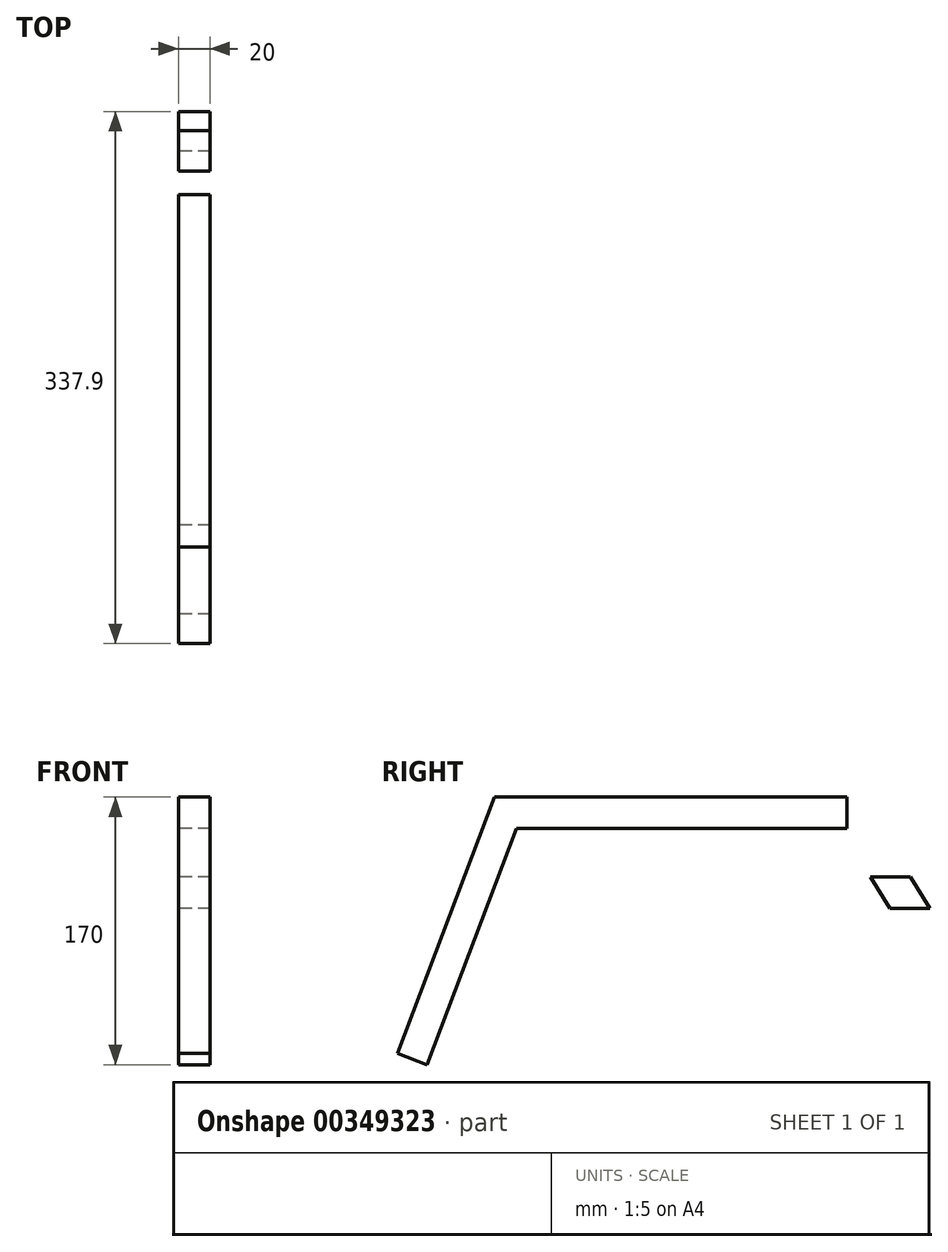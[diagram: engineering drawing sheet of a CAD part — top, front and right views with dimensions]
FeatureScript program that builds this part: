
annotation { "Feature Type Name" : "Feature", "Feature Type Description" : "" }
export const myFeature = defineFeature(function(context is Context, id is Id, definition is map)
    precondition{}
    {
        {
            var Q0;
            Q0=qCreatedBy(makeId("Right.planeOp"),FACE);
            var sketch = newSketch(context, id + "F0", { "sketchPlane" : qUnion([Q0])});
            skLineSegment(sketch, "E0", {"start": v(241, -95.83) * mm, "end": v(224.34, -106.9) * mm});
            skLineSegment(sketch, "E1", {"start": v(241, -95.83) * mm, "end": v(217.72, -95.83) * mm});
            skLineSegment(sketch, "E2", {"start": v(241, -95.83) * mm, "end": v(-76.2, -95.83) * mm});
            skLineSegment(sketch, "E3", {"start": v(-76.2, -95.83) * mm, "end": v(-76.2, 44.17) * mm});
            skLineSegment(sketch, "E4", {"start": v(-76.2, 44.17) * mm, "end": v(-76.2, 24.17) * mm});
            skLineSegment(sketch, "E5", {"start": v(-76.2, 24.17) * mm, "end": v(328.64, 24.17) * mm});
            skLineSegment(sketch, "E6", {"start": v(-76.2, 44.17) * mm, "end": v(348.84, 44.17) * mm});
            skLineSegment(sketch, "E7", {"start": v(241, -95.83) * mm, "end": v(139.09, 70.9) * mm});
            skLineSegment(sketch, "E8", {"start": v(224.34, -106.9) * mm, "end": v(129.89, 44.17) * mm});
            skLineSegment(sketch, "E9", {"start": v(129.89, 44.17) * mm, "end": v(148.48, 55.53) * mm});
            skSolve(sketch);
        }
        {
            var Q0;
            Q0=qCreatedBy(makeId("Right.planeOp"),FACE);
            var sketch = newSketch(context, id + "F1", { "sketchPlane" : qUnion([Q0])});
            skLineSegment(sketch, "E10.bottom", {"start": v(-95, 75) * mm, "end": v(95, 75) * mm});
            skLineSegment(sketch, "E10.top", {"start": v(-95, -75) * mm, "end": v(95, -75) * mm});
            skLineSegment(sketch, "E10.left", {"start": v(-95, 75) * mm, "end": v(-95, -75) * mm});
            skLineSegment(sketch, "E10.right", {"start": v(95, 75) * mm, "end": v(95, -75) * mm});
            skPoint(sketch, "E10.middle", {"position": v(0, 0) * mm});
            skLineSegment(sketch, "E11", {"start": v(-95, 75) * mm, "end": v(-151.54, -75) * mm});
            skLineSegment(sketch, "E12", {"start": v(-151.54, -75) * mm, "end": v(-170.25, -67.95) * mm});
            skLineSegment(sketch, "E13", {"start": v(-49.15, 75) * mm, "end": v(-49.15, 95) * mm});
            skLineSegment(sketch, "E14", {"start": v(-49.15, 95) * mm, "end": v(-150.32, 95) * mm});
            skLineSegment(sketch, "E15", {"start": v(-170.25, -67.95) * mm, "end": v(-97.28, 125.65) * mm});
            skLineSegment(sketch, "E16", {"start": v(-49.15, 95) * mm, "end": v(184.11, 95) * mm});
            skLineSegment(sketch, "E17", {"start": v(95, 95) * mm, "end": v(115, 95) * mm});
            skLineSegment(sketch, "E18", {"start": v(115, 95) * mm, "end": v(115, 75) * mm});
            skLineSegment(sketch, "E19", {"start": v(115, 75) * mm, "end": v(95, 75) * mm});
            skSolve(sketch);
        }
        {
            var Q0;
            {var subQ2=sQuery(id+"F1.wireOp",EDGE,"E11");Q0=makeQuery(id+"F1.imprint","IMPRINT",FACE,{"disambiguationData":[TD([[makeQuery(id+"F1.imprint","IMPRINT",EDGE,{"derivedFrom":subQ2}),-1.0]])]});}
            var Q1;
            {var subQ1=sQuery(id+"F1.wireOp",EDGE,"E13");Q1=makeQuery(id+"F1.imprint","IMPRINT",FACE,{"disambiguationData":[TD([[makeQuery(id+"F1.imprint","IMPRINT",EDGE,{"derivedFrom":subQ1}),-1.0]])]});}
            extrude(context, id + "F2", {"entities" : qUnion([Q0, Q1]), "depth" : 20 * mm});
        }
        {
            var Q0;
            {var subQ1=sQuery(id+"F0.wireOp",EDGE,"E2");var subQ7=makeQuery(id+"F0.imprint","IMPRINT",VERTEX,{"derivedFrom":subQ1});Q0=makeQuery(id+"F0.imprint","IMPRINT",FACE,{"disambiguationData":[TD([[makeQuery(id+"F0.imprint","IMPRINT",EDGE,{"disambiguationData":[TD([[subQ7,-1.0]])],"derivedFrom":subQ1}),-1.0]])]});}
            var Q1;
            {var subQ0=sQuery(id+"F0.wireOp",EDGE,"E4");Q1=makeQuery(id+"F0.imprint","IMPRINT",FACE,{"disambiguationData":[TD([[makeQuery(id+"F0.imprint","IMPRINT",EDGE,{"derivedFrom":subQ0}),1.0]])]});}
            var Q2;
            {var subQ0=sQuery(id+"F0.wireOp",EDGE,"E7");var subQ1=sQuery(id+"F0.wireOp",EDGE,"E5");var subQ2=makeQuery(id+"F0.imprint","INTERSECT",VERTEX,{"derivedFrom":[subQ1,subQ0]});Q2=makeQuery(id+"F0.imprint","IMPRINT",FACE,{"disambiguationData":[TD([[makeQuery(id+"F0.imprint","IMPRINT",EDGE,{"disambiguationData":[TD([[subQ2,1.0]])],"derivedFrom":subQ1}),1.0]])]});}
            extrude(context, id + "F3", {"entities" : qUnion([Q0, Q1, Q2]), "depth" : 20 * mm});
        }
    });
